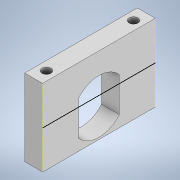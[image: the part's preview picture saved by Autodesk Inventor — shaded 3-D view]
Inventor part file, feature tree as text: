
AUTODESK INVENTOR PART (.ipt)
format: ipt  version: 2020 (Build 240168000, 168)  size: 124,416 bytes
history: native  units: mm
features: sketch x3, extrude x2, other x1, projected_geometry x1
ambient origin geometry x8: Origin, YZ Plane, XZ Plane, XY Plane, X Axis, Y Axis, Z Axis, Center Point
bodies: Body1 (feature_tree)
feature tree (7):
  other  "Твердое тело1"
  extrude  "Выдавливание1"  Depth=44.0mm
  extrude  "Выдавливание2"  Depth=30.0mm TaperAngle=0.0deg
  sketch  "Эскиз3"
  sketch  "Эскиз1"
  sketch  "Эскиз2"
  projected_geometry  "Спроецированная петля1"
